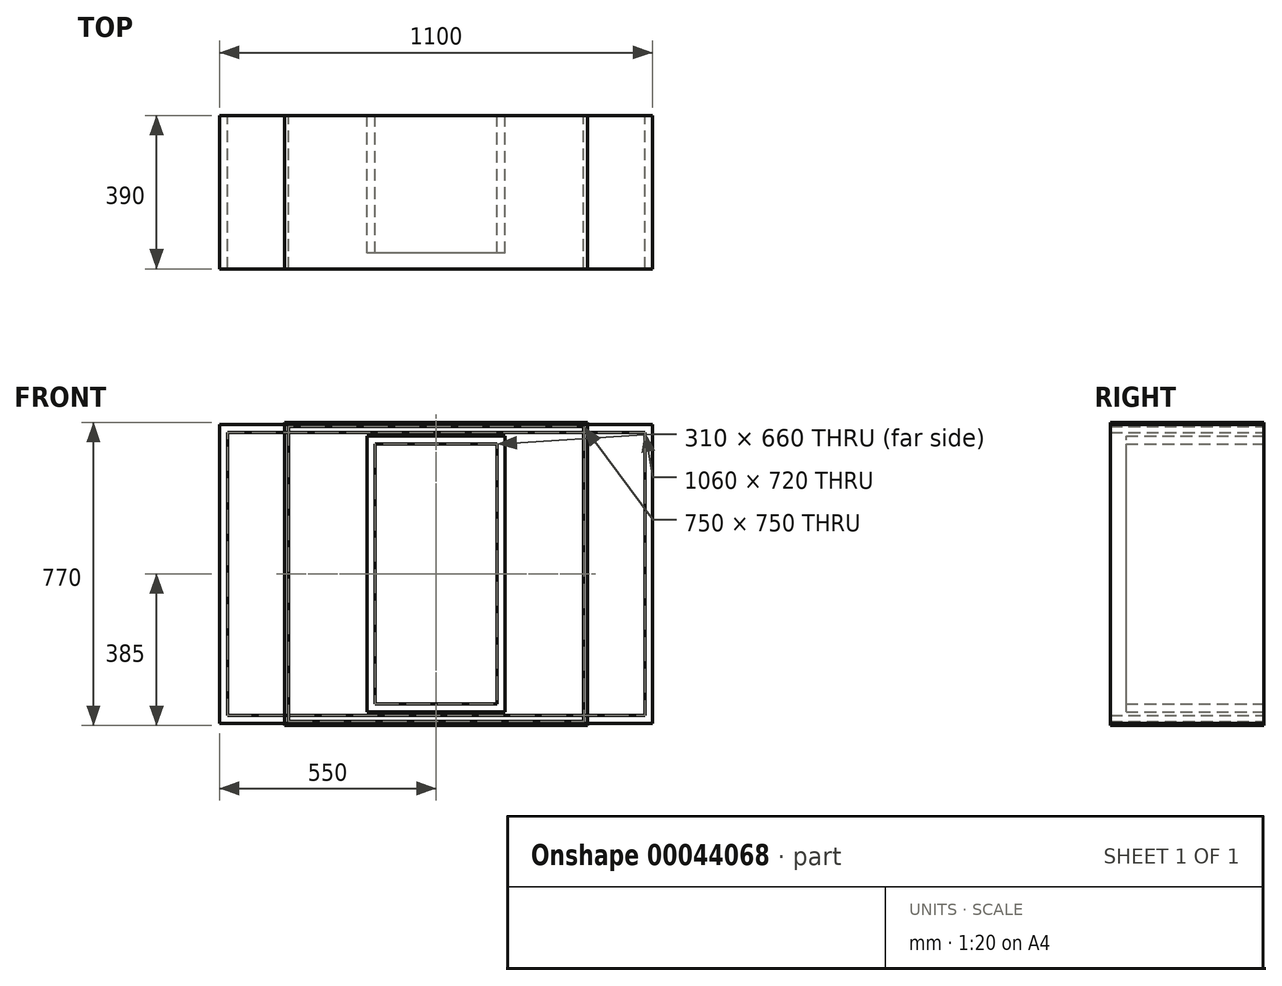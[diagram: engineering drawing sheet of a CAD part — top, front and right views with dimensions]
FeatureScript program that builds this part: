
annotation { "Feature Type Name" : "Feature", "Feature Type Description" : "" }
export const myFeature = defineFeature(function(context is Context, id is Id, definition is map)
    precondition{}
    {
        {
            var Q0;
            Q0=qCreatedBy(makeId("Front.planeOp"), FACE);
            var sketch = newSketch(context, id + "F0", { "sketchPlane" : qUnion([Q0])});
            skLineSegment(sketch, "E0.bottom", {"start": v(385, -385) * mm, "end": v(-385, -385) * mm});
            skLineSegment(sketch, "E0.top", {"start": v(385, 385) * mm, "end": v(-385, 385) * mm});
            skLineSegment(sketch, "E0.left", {"start": v(385, -385) * mm, "end": v(385, 385) * mm});
            skLineSegment(sketch, "E0.right", {"start": v(-385, -385) * mm, "end": v(-385, 385) * mm});
            skPoint(sketch, "E0.middle", {"position": v(0, 0) * mm});
            skLineSegment(sketch, "E1.0", {"start": v(-375, -375) * mm, "end": v(-375, 375) * mm});
            skLineSegment(sketch, "E1.1", {"start": v(375, -375) * mm, "end": v(-375, -375) * mm});
            skLineSegment(sketch, "E1.2", {"start": v(375, -375) * mm, "end": v(375, 375) * mm});
            skLineSegment(sketch, "E1.3", {"start": v(375, 375) * mm, "end": v(-375, 375) * mm});
            skSolve(sketch);
        }
        {
            var Q0;
            Q0 = qSketchRegion(id + "F0", true);
            extrude(context, id + "F1", {"entities" : qUnion([Q0]), "depth" : 390 * mm, "offsetDistance" : 25 * mm});
        }
        {
            var Q0;
            Q0=qCreatedBy(makeId("Front.planeOp"), FACE);
            var sketch = newSketch(context, id + "F2", { "sketchPlane" : qUnion([Q0])});
            skLineSegment(sketch, "E2.bottom", {"start": v(550, -380) * mm, "end": v(-550, -380) * mm});
            skLineSegment(sketch, "E2.top", {"start": v(550, 380) * mm, "end": v(-550, 380) * mm});
            skLineSegment(sketch, "E2.left", {"start": v(550, -380) * mm, "end": v(550, 380) * mm});
            skLineSegment(sketch, "E2.right", {"start": v(-550, -380) * mm, "end": v(-550, 380) * mm});
            skPoint(sketch, "E2.middle", {"position": v(0, 0) * mm});
            skLineSegment(sketch, "E3.0", {"start": v(-530, -360) * mm, "end": v(-530, 360) * mm});
            skLineSegment(sketch, "E3.1", {"start": v(530, -360) * mm, "end": v(-530, -360) * mm});
            skLineSegment(sketch, "E3.2", {"start": v(530, -360) * mm, "end": v(530, 360) * mm});
            skLineSegment(sketch, "E3.3", {"start": v(530, 360) * mm, "end": v(-530, 360) * mm});
            skSolve(sketch);
        }
        {
            var Q0;
            Q0 = qSketchRegion(id + "F2", true);
            extrude(context, id + "F3", {"entities" : qUnion([Q0]), "depth" : 390 * mm, "offsetDistance" : 25 * mm});
        }
        {
            var Q0;
            Q0=qCreatedBy(makeId("Front.planeOp"), FACE);
            var sketch = newSketch(context, id + "F4", { "sketchPlane" : qUnion([Q0])});
            skLineSegment(sketch, "E4.bottom", {"start": v(175, -350) * mm, "end": v(-175, -350) * mm});
            skLineSegment(sketch, "E4.top", {"start": v(175, 350) * mm, "end": v(-175, 350) * mm});
            skLineSegment(sketch, "E4.left", {"start": v(175, -350) * mm, "end": v(175, 350) * mm});
            skLineSegment(sketch, "E4.right", {"start": v(-175, -350) * mm, "end": v(-175, 350) * mm});
            skPoint(sketch, "E4.middle", {"position": v(0, 0) * mm});
            skLineSegment(sketch, "E5.0", {"start": v(-155, -330) * mm, "end": v(-155, 330) * mm});
            skLineSegment(sketch, "E5.1", {"start": v(155, -330) * mm, "end": v(-155, -330) * mm});
            skLineSegment(sketch, "E5.2", {"start": v(155, -330) * mm, "end": v(155, 330) * mm});
            skLineSegment(sketch, "E5.3", {"start": v(155, 330) * mm, "end": v(-155, 330) * mm});
            skSolve(sketch);
        }
        {
            var Q0;
            Q0 = qSketchRegion(id + "F4", true);
            extrude(context, id + "F5", {"entities" : qUnion([Q0]), "depth" : 350 * mm, "offsetDistance" : 25 * mm});
        }
    });
